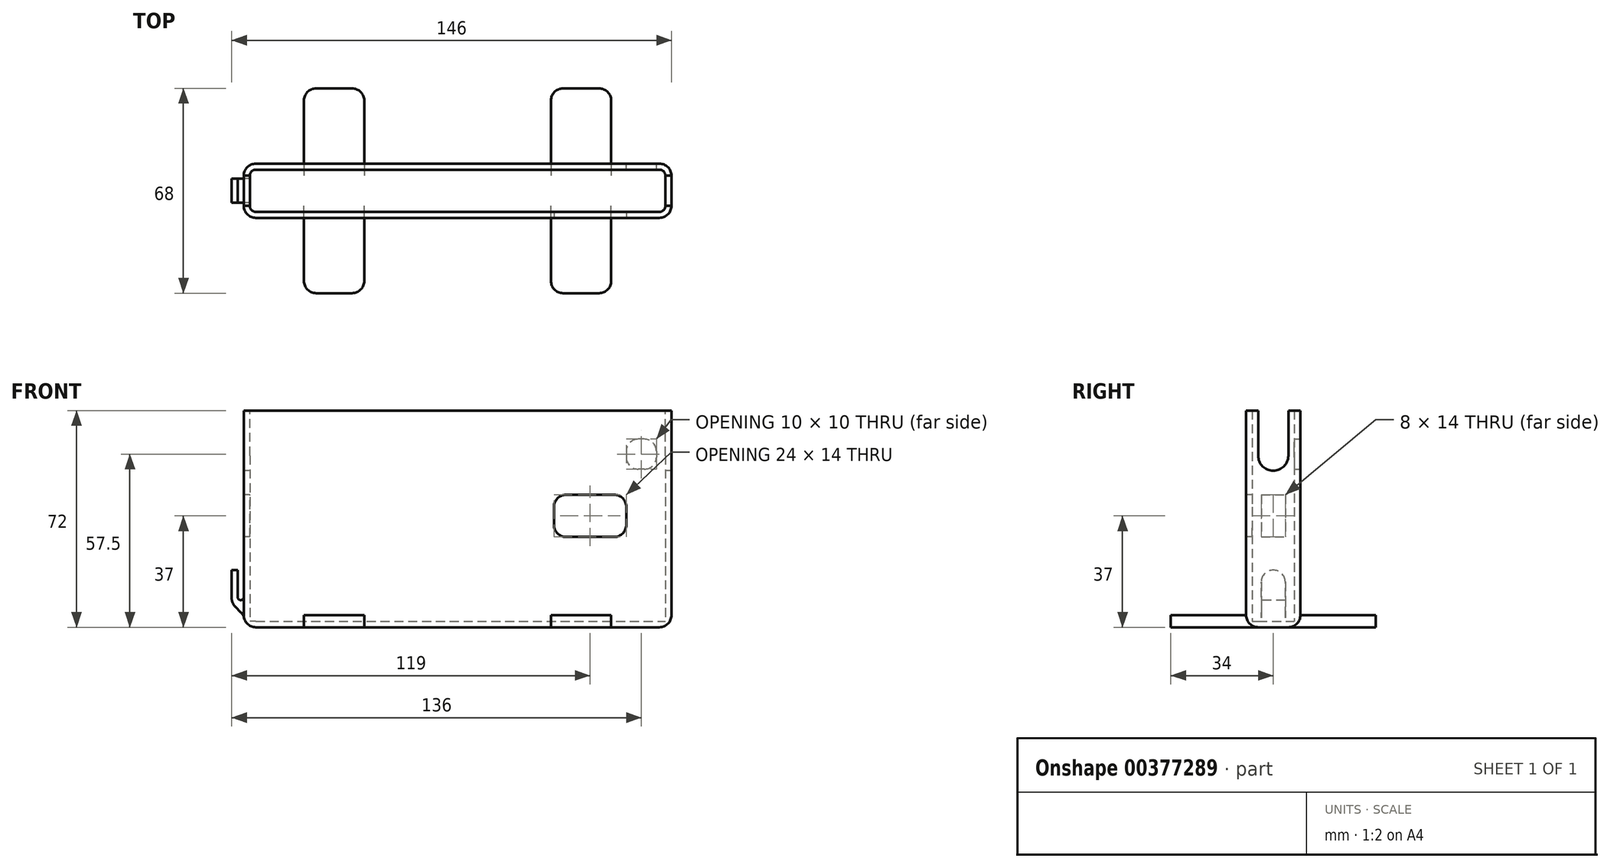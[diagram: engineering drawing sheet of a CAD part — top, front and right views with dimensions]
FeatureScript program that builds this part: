
annotation { "Feature Type Name" : "Feature", "Feature Type Description" : "" }
export const myFeature = defineFeature(function(context is Context, id is Id, definition is map)
    precondition{}
    {
        {
            var Q0;
            Q0=qCreatedBy(makeId("Top.planeOp"),FACE);
            var sketch = newSketch(context, id + "F0", { "sketchPlane" : qUnion([Q0])});
            skLineSegment(sketch, "E0.bottom", {"start": v(0, 0) * mm, "end": v(142, 0) * mm});
            skLineSegment(sketch, "E0.top", {"start": v(0, 18) * mm, "end": v(142, 18) * mm});
            skLineSegment(sketch, "E0.left", {"start": v(0, 0) * mm, "end": v(0, 18) * mm});
            skLineSegment(sketch, "E0.right", {"start": v(142, 0) * mm, "end": v(142, 18) * mm});
            skSolve(sketch);
        }
        {
            var Q0;
            Q0=qSketchRegion(id+"F0",true);
            extrude(context, id + "F1", {"entities" : qUnion([Q0]), "depth" : 2 * mm});
        }
        {
            var Q0;
            Q0=makeQuery(id+"F1.opExtrude","CAP_FACE",FACE,{"disambiguationData":[OSD([sQuery(id+"F0.wireOp",EDGE,"E0.bottom"),sQuery(id+"F0.wireOp",EDGE,"E0.top"),sQuery(id+"F0.wireOp",EDGE,"E0.left"),sQuery(id+"F0.wireOp",EDGE,"E0.right")])],"isStart":false});
            var sketch = newSketch(context, id + "F2", { "sketchPlane" : qUnion([Q0])});
            skLineSegment(sketch, "E1.0", {"start": v(0, 18) * mm, "end": v(142, 18) * mm});
            skLineSegment(sketch, "E1.1", {"start": v(0, 0) * mm, "end": v(0, 18) * mm});
            skLineSegment(sketch, "E1.2", {"start": v(0, 0) * mm, "end": v(142, 0) * mm});
            skLineSegment(sketch, "E1.3", {"start": v(142, 0) * mm, "end": v(142, 18) * mm});
            skLineSegment(sketch, "E2.0", {"start": v(2, 16) * mm, "end": v(140, 16) * mm});
            skLineSegment(sketch, "E2.1", {"start": v(2, 2) * mm, "end": v(2, 16) * mm});
            skLineSegment(sketch, "E2.2", {"start": v(2, 2) * mm, "end": v(140, 2) * mm});
            skLineSegment(sketch, "E2.3", {"start": v(140, 2) * mm, "end": v(140, 16) * mm});
            skSolve(sketch);
        }
        {
            var Q0;
            Q0=qSketchRegion(id+"F2",true);
            extrude(context, id + "F3", {"entities" : qUnion([Q0]), "operationType" : NewBodyOperationType.ADD, "depth" : 70 * mm});
        }
        {
            var Q0;
            Q0=makeQuery(id+"F3.opExtrude","SWEPT_EDGE",EDGE,{"disambiguationData":[OSD([sQuery(id+"F2.wireOp",EDGE,"E2.1"),sQuery(id+"F2.wireOp",EDGE,"E2.2")])]});
            var Q1;
            Q1=makeQuery(id+"F3.opExtrude","SWEPT_EDGE",EDGE,{"disambiguationData":[OSD([sQuery(id+"F2.wireOp",EDGE,"E2.0"),sQuery(id+"F2.wireOp",EDGE,"E2.1")])]});
            var Q2;
            Q2=makeQuery(id+"F3.opExtrude","SWEPT_EDGE",EDGE,{"disambiguationData":[OSD([sQuery(id+"F2.wireOp",EDGE,"E2.0"),sQuery(id+"F2.wireOp",EDGE,"E2.3")])]});
            var Q3;
            Q3=makeQuery(id+"F3.opExtrude","SWEPT_EDGE",EDGE,{"disambiguationData":[OSD([sQuery(id+"F2.wireOp",EDGE,"E2.2"),sQuery(id+"F2.wireOp",EDGE,"E2.3")])]});
            var Q4;
            Q4=makeQuery(id+"F3.opExtrude","CAP_EDGE",EDGE,{"disambiguationData":[OSD([sQuery(id+"F2.wireOp",EDGE,"E2.2")])],"isStart":true});
            var Q5;
            Q5=makeQuery(id+"F3.opExtrude","CAP_EDGE",EDGE,{"disambiguationData":[OSD([sQuery(id+"F2.wireOp",EDGE,"E2.3")])],"isStart":true});
            var Q6;
            Q6=makeQuery(id+"F3.opExtrude","CAP_EDGE",EDGE,{"disambiguationData":[OSD([sQuery(id+"F2.wireOp",EDGE,"E2.0")])],"isStart":true});
            var Q7;
            Q7=makeQuery(id+"F3.opExtrude","CAP_EDGE",EDGE,{"disambiguationData":[OSD([sQuery(id+"F2.wireOp",EDGE,"E2.1")])],"isStart":true});
            fillet(context, id + "F4", {"entities" : qUnion([Q0, Q1, Q2, Q3, Q4, Q5, Q6, Q7]), "radius" : 2 * mm, "tangentPropagation" : true, "allowEdgeOverflow" : false});
        }
        {
            var Q0;
            Q0=makeQuery(id+"F3.boolean.opBoolean","MERGE",EDGE,{"derivedFrom":[makeQuery(id+"F1.opExtrude","SWEPT_EDGE",EDGE,{"disambiguationData":[OSD([sQuery(id+"F0.wireOp",EDGE,"E0.bottom"),sQuery(id+"F0.wireOp",EDGE,"E0.left")])]}),makeQuery(id+"F3.opExtrude","SWEPT_EDGE",EDGE,{"disambiguationData":[OSD([sQuery(id+"F2.wireOp",EDGE,"E1.1"),sQuery(id+"F2.wireOp",EDGE,"E1.2")])]})]});
            var Q1;
            Q1=makeQuery(id+"F3.boolean.opBoolean","MERGE",EDGE,{"derivedFrom":[makeQuery(id+"F1.opExtrude","SWEPT_EDGE",EDGE,{"disambiguationData":[OSD([sQuery(id+"F0.wireOp",EDGE,"E0.top"),sQuery(id+"F0.wireOp",EDGE,"E0.left")])]}),makeQuery(id+"F3.opExtrude","SWEPT_EDGE",EDGE,{"disambiguationData":[OSD([sQuery(id+"F2.wireOp",EDGE,"E1.0"),sQuery(id+"F2.wireOp",EDGE,"E1.1")])]})]});
            var Q2;
            Q2=makeQuery(id+"F3.boolean.opBoolean","MERGE",EDGE,{"derivedFrom":[makeQuery(id+"F1.opExtrude","SWEPT_EDGE",EDGE,{"disambiguationData":[OSD([sQuery(id+"F0.wireOp",EDGE,"E0.top"),sQuery(id+"F0.wireOp",EDGE,"E0.right")])]}),makeQuery(id+"F3.opExtrude","SWEPT_EDGE",EDGE,{"disambiguationData":[OSD([sQuery(id+"F2.wireOp",EDGE,"E1.0"),sQuery(id+"F2.wireOp",EDGE,"E1.3")])]})]});
            var Q3;
            Q3=makeQuery(id+"F3.boolean.opBoolean","MERGE",EDGE,{"derivedFrom":[makeQuery(id+"F1.opExtrude","SWEPT_EDGE",EDGE,{"disambiguationData":[OSD([sQuery(id+"F0.wireOp",EDGE,"E0.bottom"),sQuery(id+"F0.wireOp",EDGE,"E0.right")])]}),makeQuery(id+"F3.opExtrude","SWEPT_EDGE",EDGE,{"disambiguationData":[OSD([sQuery(id+"F2.wireOp",EDGE,"E1.2"),sQuery(id+"F2.wireOp",EDGE,"E1.3")])]})]});
            var Q4;
            Q4=makeQuery(id+"F1.opExtrude","CAP_EDGE",EDGE,{"disambiguationData":[OSD([sQuery(id+"F0.wireOp",EDGE,"E0.bottom")])],"isStart":true});
            var Q5;
            Q5=makeQuery(id+"F1.opExtrude","CAP_EDGE",EDGE,{"disambiguationData":[OSD([sQuery(id+"F0.wireOp",EDGE,"E0.left")])],"isStart":true});
            var Q6;
            Q6=makeQuery(id+"F1.opExtrude","CAP_EDGE",EDGE,{"disambiguationData":[OSD([sQuery(id+"F0.wireOp",EDGE,"E0.top")])],"isStart":true});
            var Q7;
            Q7=makeQuery(id+"F1.opExtrude","CAP_EDGE",EDGE,{"disambiguationData":[OSD([sQuery(id+"F0.wireOp",EDGE,"E0.right")])],"isStart":true});
            fillet(context, id + "F5", {"entities" : qUnion([Q0, Q1, Q2, Q3, Q4, Q5, Q6, Q7]), "radius" : 4 * mm, "tangentPropagation" : true, "allowEdgeOverflow" : false});
        }
        {
            var Q0;
            Q0=makeQuery(id+"F3.boolean.opBoolean","MERGE",FACE,{"derivedFrom":[makeQuery(id+"F1.opExtrude","SWEPT_FACE",FACE,{"disambiguationData":[OSD([sQuery(id+"F0.wireOp",EDGE,"E0.left")])]}),makeQuery(id+"F3.opExtrude","SWEPT_FACE",FACE,{"disambiguationData":[OSD([sQuery(id+"F2.wireOp",EDGE,"E1.1")])]})]});
            var sketch = newSketch(context, id + "F6", { "sketchPlane" : qUnion([Q0])});
            skLineSegment(sketch, "E3", {"start": v(-9, 72) * mm, "end": v(-9, 57) * mm, "construction": true});
            skArc(sketch, "E4.0.startCap", {"start": v(-14, 72) * mm, "mid": v(-9, 77) * mm, "end": v(-4, 72) * mm});
            skArc(sketch, "E4.0.endCap", {"start": v(-4, 57) * mm, "mid": v(-9, 52) * mm, "end": v(-14, 57) * mm});
            skLineSegment(sketch, "E4.0.left", {"start": v(-4, 72) * mm, "end": v(-4, 57) * mm});
            skLineSegment(sketch, "E4.0.right", {"start": v(-14, 72) * mm, "end": v(-14, 57) * mm});
            skSolve(sketch);
        }
        {
            var Q0;
            Q0=qSketchRegion(id+"F6",true);
            extrude(context, id + "F7", {"entities" : qUnion([Q0]), "operationType" : NewBodyOperationType.REMOVE, "endBound" : BoundingType.THROUGH_ALL, "oppositeDirection" : true, "depth" : 25 * mm});
        }
        {
            var Q0;
            Q0=makeQuery(id+"F3.boolean.opBoolean","MERGE",FACE,{"derivedFrom":[makeQuery(id+"F1.opExtrude","SWEPT_FACE",FACE,{"disambiguationData":[OSD([sQuery(id+"F0.wireOp",EDGE,"E0.bottom")])]}),makeQuery(id+"F3.opExtrude","SWEPT_FACE",FACE,{"disambiguationData":[OSD([sQuery(id+"F2.wireOp",EDGE,"E1.2")])]})]});
            var sketch = newSketch(context, id + "F8", { "sketchPlane" : qUnion([Q0])});
            skLineSegment(sketch, "E5.bottom", {"start": v(107, 44) * mm, "end": v(123, 44) * mm});
            skLineSegment(sketch, "E5.top", {"start": v(107, 30) * mm, "end": v(123, 30) * mm});
            skLineSegment(sketch, "E5.left", {"start": v(103, 40) * mm, "end": v(103, 34) * mm});
            skLineSegment(sketch, "E5.right", {"start": v(127, 40) * mm, "end": v(127, 34) * mm});
            skPoint(sketch, "E6", {"position": v(103, 37) * mm});
            skPoint(sketch, "E7.visualSharp", {"position": v(103, 44) * mm});
            skArc(sketch, "E7.filletArc", {"start": v(107, 44) * mm, "mid": v(104.17, 42.83) * mm, "end": v(103, 40) * mm});
            skPoint(sketch, "E8.visualSharp", {"position": v(127, 44) * mm});
            skArc(sketch, "E8.filletArc", {"start": v(127, 40) * mm, "mid": v(125.83, 42.83) * mm, "end": v(123, 44) * mm});
            skPoint(sketch, "E9.visualSharp", {"position": v(127, 30) * mm});
            skArc(sketch, "E9.filletArc", {"start": v(123, 30) * mm, "mid": v(125.83, 31.17) * mm, "end": v(127, 34) * mm});
            skPoint(sketch, "E10.visualSharp", {"position": v(103, 30) * mm});
            skArc(sketch, "E10.filletArc", {"start": v(103, 34) * mm, "mid": v(104.17, 31.17) * mm, "end": v(107, 30) * mm});
            skPoint(sketch, "E11", {"position": v(115, 44) * mm});
            skSolve(sketch);
        }
        {
            var Q0;
            Q0=qSketchRegion(id+"F8",true);
            extrude(context, id + "F9", {"entities" : qUnion([Q0]), "operationType" : NewBodyOperationType.REMOVE, "endBound" : BoundingType.UP_TO_NEXT, "oppositeDirection" : true, "depth" : 25 * mm});
        }
        {
            var Q0;
            Q0=makeQuery(id+"F3.boolean.opBoolean","MERGE",FACE,{"derivedFrom":[makeQuery(id+"F1.opExtrude","SWEPT_FACE",FACE,{"disambiguationData":[OSD([sQuery(id+"F0.wireOp",EDGE,"E0.left")])]}),makeQuery(id+"F3.opExtrude","SWEPT_FACE",FACE,{"disambiguationData":[OSD([sQuery(id+"F2.wireOp",EDGE,"E1.1")])]})]});
            var sketch = newSketch(context, id + "F10", { "sketchPlane" : qUnion([Q0])});
            skLineSegment(sketch, "E12.bottom", {"start": v(-13, 19) * mm, "end": v(-5, 19) * mm});
            skLineSegment(sketch, "E12.top", {"start": v(-13, 4) * mm, "end": v(-5, 4) * mm});
            skLineSegment(sketch, "E12.left", {"start": v(-13, 19) * mm, "end": v(-13, 4) * mm});
            skLineSegment(sketch, "E12.right", {"start": v(-5, 19) * mm, "end": v(-5, 4) * mm});
            skPoint(sketch, "E13", {"position": v(-9, 4) * mm});
            skSolve(sketch);
        }
        {
            var Q0;
            Q0=qSketchRegion(id+"F10",true);
            extrude(context, id + "F11", {"entities" : qUnion([Q0]), "operationType" : NewBodyOperationType.ADD, "depth" : 4 * mm});
        }
        {
            var Q0;
            Q0=makeQuery(id+"F11.opExtrude","CAP_EDGE",EDGE,{"disambiguationData":[OSD([sQuery(id+"F10.wireOp",EDGE,"E12.top")])],"isStart":false});
            chamfer(context, id + "F12", {"entities" : qUnion([Q0]), "width" : 4 * mm, "tangentPropagation" : true});
        }
        {
            var Q0;
            Q0=makeQuery(id+"F11.opExtrude","SWEPT_FACE",FACE,{"disambiguationData":[OSD([sQuery(id+"F10.wireOp",EDGE,"E12.bottom")])]});
            var sketch = newSketch(context, id + "F13", { "sketchPlane" : qUnion([Q0])});
            skLineSegment(sketch, "E14.bottom", {"start": v(-2, 13) * mm, "end": v(0, 13) * mm});
            skLineSegment(sketch, "E14.top", {"start": v(-2, 5) * mm, "end": v(0, 5) * mm});
            skLineSegment(sketch, "E14.left", {"start": v(0, 5) * mm, "end": v(0, 13) * mm});
            skLineSegment(sketch, "E14.right", {"start": v(-2, 5) * mm, "end": v(-2, 13) * mm});
            skSolve(sketch);
        }
        {
            var Q0;
            Q0=qSketchRegion(id+"F13",true);
            extrude(context, id + "F14", {"entities" : qUnion([Q0]), "operationType" : NewBodyOperationType.REMOVE, "oppositeDirection" : true, "depth" : 10 * mm});
        }
        {
            var Q0;
            Q0=makeQuery(id+"F11.opExtrude","SWEPT_EDGE",EDGE,{"disambiguationData":[OSD([sQuery(id+"F10.wireOp",EDGE,"E12.bottom"),sQuery(id+"F10.wireOp",EDGE,"E12.left")])]});
            var Q1;
            Q1=makeQuery(id+"F11.opExtrude","SWEPT_EDGE",EDGE,{"disambiguationData":[OSD([sQuery(id+"F10.wireOp",EDGE,"E12.bottom"),sQuery(id+"F10.wireOp",EDGE,"E12.right")])]});
            var Q2;
            {var subQ0=sQuery(id+"F10.wireOp",EDGE,"E12.top");Q2=makeQuery(id+"F12.opChamfer","BLEND_EDGE",EDGE,{"blendedFrom":[makeQuery(id+"F11.opExtrude","CAP_EDGE",EDGE,{"disambiguationData":[OSD([subQ0])],"isStart":false}),makeQuery(id+"F11.opExtrude","CAP_FACE",FACE,{"disambiguationData":[OSD([sQuery(id+"F10.wireOp",EDGE,"E12.bottom"),subQ0,sQuery(id+"F10.wireOp",EDGE,"E12.left"),sQuery(id+"F10.wireOp",EDGE,"E12.right")])],"isStart":false})],"blendedInto":[makeQuery(id+"F11.opExtrude","CAP_FACE",FACE,{"disambiguationData":[OSD([sQuery(id+"F10.wireOp",EDGE,"E12.bottom"),subQ0,sQuery(id+"F10.wireOp",EDGE,"E12.left"),sQuery(id+"F10.wireOp",EDGE,"E12.right")])],"isStart":false})]});}
            var Q3;
            Q3=makeQuery(id+"F12.opChamfer","BLEND_EDGE",EDGE,{"blendedFrom":[makeQuery(id+"F11.opExtrude","CAP_EDGE",EDGE,{"disambiguationData":[OSD([sQuery(id+"F10.wireOp",EDGE,"E12.top")])],"isStart":false}),makeQuery(id+"F5.opFillet","BLEND_FACE",FACE,{"disambiguationData":[OSD([sQuery(id+"F0.wireOp",EDGE,"E0.right")])]})],"blendedInto":[makeQuery(id+"F5.opFillet","BLEND_FACE",FACE,{"disambiguationData":[OSD([sQuery(id+"F0.wireOp",EDGE,"E0.right")])]})]});
            var Q4;
            Q4=makeQuery(id+"F12.opChamfer","BLEND_EDGE",EDGE,{"blendedFrom":[makeQuery(id+"F11.opExtrude","CAP_EDGE",EDGE,{"disambiguationData":[OSD([sQuery(id+"F10.wireOp",EDGE,"E12.top")])],"isStart":false}),makeQuery(id+"F5.opFillet","BLEND_FACE",FACE,{"disambiguationData":[OSD([sQuery(id+"F0.wireOp",EDGE,"E0.left")])]})],"blendedInto":[makeQuery(id+"F5.opFillet","BLEND_FACE",FACE,{"disambiguationData":[OSD([sQuery(id+"F0.wireOp",EDGE,"E0.left")])]})]});
            fillet(context, id + "F15", {"entities" : qUnion([Q0, Q1, Q2, Q3, Q4]), "radius" : 4 * mm, "tangentPropagation" : true, "allowEdgeOverflow" : false});
        }
        {
            var Q0;
            Q0=makeQuery(id+"F14.boolean.opBoolean","COPY",EDGE,{"derivedFrom":makeQuery(id+"F14.opExtrude","CAP_EDGE",EDGE,{"disambiguationData":[OSD([sQuery(id+"F13.wireOp",EDGE,"E14.right")])],"isStart":false})});
            var Q1;
            Q1=makeQuery(id+"F14.boolean.opBoolean","COPY",EDGE,{"derivedFrom":makeQuery(id+"F14.opExtrude","CAP_EDGE",EDGE,{"disambiguationData":[OSD([sQuery(id+"F13.wireOp",EDGE,"E14.left")])],"isStart":false})});
            fillet(context, id + "F16", {"entities" : qUnion([Q0, Q1]), "radius" : 1 * mm, "tangentPropagation" : true, "allowEdgeOverflow" : false});
        }
        {
            var Q0;
            Q0=makeQuery(id+"F3.boolean.opBoolean","MERGE",FACE,{"derivedFrom":[makeQuery(id+"F1.opExtrude","SWEPT_FACE",FACE,{"disambiguationData":[OSD([sQuery(id+"F0.wireOp",EDGE,"E0.top")])]}),makeQuery(id+"F3.opExtrude","SWEPT_FACE",FACE,{"disambiguationData":[OSD([sQuery(id+"F2.wireOp",EDGE,"E1.0")])]})]});
            var sketch = newSketch(context, id + "F17", { "sketchPlane" : qUnion([Q0])});
            skLineSegment(sketch, "E15.bottom", {"start": v(-133, 62.5) * mm, "end": v(-131, 62.5) * mm});
            skLineSegment(sketch, "E15.top", {"start": v(-133, 52.5) * mm, "end": v(-131, 52.5) * mm});
            skLineSegment(sketch, "E15.left", {"start": v(-137, 58.5) * mm, "end": v(-137, 56.5) * mm});
            skLineSegment(sketch, "E15.right", {"start": v(-127, 58.5) * mm, "end": v(-127, 56.5) * mm});
            skPoint(sketch, "E16.visualSharp", {"position": v(-137, 62.5) * mm});
            skArc(sketch, "E16.filletArc", {"start": v(-133, 62.5) * mm, "mid": v(-135.83, 61.33) * mm, "end": v(-137, 58.5) * mm});
            skPoint(sketch, "E17.visualSharp", {"position": v(-127, 62.5) * mm});
            skArc(sketch, "E17.filletArc", {"start": v(-127, 58.5) * mm, "mid": v(-128.17, 61.33) * mm, "end": v(-131, 62.5) * mm});
            skPoint(sketch, "E18.visualSharp", {"position": v(-127, 52.5) * mm});
            skArc(sketch, "E18.filletArc", {"start": v(-131, 52.5) * mm, "mid": v(-128.17, 53.67) * mm, "end": v(-127, 56.5) * mm});
            skPoint(sketch, "E19.visualSharp", {"position": v(-137, 52.5) * mm});
            skArc(sketch, "E19.filletArc", {"start": v(-137, 56.5) * mm, "mid": v(-135.83, 53.67) * mm, "end": v(-133, 52.5) * mm});
            skPoint(sketch, "E20", {"position": v(-132, 62.5) * mm});
            skPoint(sketch, "E21", {"position": v(-127, 57.5) * mm});
            skSolve(sketch);
        }
        {
            var Q0;
            Q0=qSketchRegion(id+"F17",true);
            extrude(context, id + "F18", {"entities" : qUnion([Q0]), "operationType" : NewBodyOperationType.REMOVE, "endBound" : BoundingType.UP_TO_NEXT, "oppositeDirection" : true, "depth" : 25 * mm});
        }
        {
            var Q0;
            Q0=makeQuery(id+"F3.boolean.opBoolean","MERGE",FACE,{"derivedFrom":[makeQuery(id+"F1.opExtrude","SWEPT_FACE",FACE,{"disambiguationData":[OSD([sQuery(id+"F0.wireOp",EDGE,"E0.left")])]}),makeQuery(id+"F3.opExtrude","SWEPT_FACE",FACE,{"disambiguationData":[OSD([sQuery(id+"F2.wireOp",EDGE,"E1.1")])]})]});
            var sketch = newSketch(context, id + "F19", { "sketchPlane" : qUnion([Q0])});
            skLineSegment(sketch, "E22.bottom", {"start": v(-5, 44) * mm, "end": v(-13, 44) * mm});
            skLineSegment(sketch, "E22.top", {"start": v(-5, 30) * mm, "end": v(-13, 30) * mm});
            skLineSegment(sketch, "E22.left", {"start": v(-5, 44) * mm, "end": v(-5, 30) * mm});
            skLineSegment(sketch, "E22.right", {"start": v(-13, 44) * mm, "end": v(-13, 30) * mm});
            skPoint(sketch, "E22.middle", {"position": v(-9, 37) * mm});
            skLineSegment(sketch, "E23", {"start": v(-14, 30.5) * mm, "end": v(-4, 30.5) * mm, "construction": true});
            skPoint(sketch, "E24", {"position": v(-9, 30.5) * mm});
            skSolve(sketch);
        }
        {
            var Q0;
            Q0=qSketchRegion(id+"F19",true);
            extrude(context, id + "F20", {"entities" : qUnion([Q0]), "operationType" : NewBodyOperationType.REMOVE, "endBound" : BoundingType.UP_TO_NEXT, "oppositeDirection" : true, "depth" : 25 * mm});
        }
        {
            var Q0;
            Q0=makeQuery(id+"F3.boolean.opBoolean","MERGE",FACE,{"derivedFrom":[makeQuery(id+"F1.opExtrude","SWEPT_FACE",FACE,{"disambiguationData":[OSD([sQuery(id+"F0.wireOp",EDGE,"E0.top")])]}),makeQuery(id+"F3.opExtrude","SWEPT_FACE",FACE,{"disambiguationData":[OSD([sQuery(id+"F2.wireOp",EDGE,"E1.0")])]})]});
            var sketch = newSketch(context, id + "F21", { "sketchPlane" : qUnion([Q0])});
            skLineSegment(sketch, "E25.bottom", {"start": v(-122, 4) * mm, "end": v(-102, 4) * mm});
            skLineSegment(sketch, "E25.top", {"start": v(-122, 0) * mm, "end": v(-102, 0) * mm});
            skLineSegment(sketch, "E25.left", {"start": v(-122, 4) * mm, "end": v(-122, 0) * mm});
            skLineSegment(sketch, "E25.right", {"start": v(-102, 4) * mm, "end": v(-102, 0) * mm});
            skLineSegment(sketch, "E26.bottom", {"start": v(-40, 4) * mm, "end": v(-20, 4) * mm});
            skLineSegment(sketch, "E26.top", {"start": v(-40, 0) * mm, "end": v(-20, 0) * mm});
            skLineSegment(sketch, "E26.left", {"start": v(-40, 4) * mm, "end": v(-40, 0) * mm});
            skLineSegment(sketch, "E26.right", {"start": v(-20, 4) * mm, "end": v(-20, 0) * mm});
            skSolve(sketch);
        }
        {
            var Q0;
            Q0 = qSketchRegion(id + "F21", true);
            var Q1;
            Q1=makeQuery(id+"F1.opExtrude","SWEPT_BODY",BODY,{"disambiguationData":[OSD([sQuery(id+"F0.wireOp",EDGE,"E0.bottom"),sQuery(id+"F0.wireOp",EDGE,"E0.top"),sQuery(id+"F0.wireOp",EDGE,"E0.left"),sQuery(id+"F0.wireOp",EDGE,"E0.right")])]});
            extrude(context, id + "F22", {"entities" : qUnion([Q0]), "operationType" : NewBodyOperationType.ADD, "depth" : 25 * mm, "hasSecondDirection" : true, "secondDirectionBound" : SecondDirectionBoundingType.UP_TO_BODY, "secondDirectionOppositeDirection" : true, "secondDirectionBoundEntityBody" : qUnion([Q1]), "secondDirectionDepth" : 25 * mm});
        }
        {
            var Q0;
            Q0=makeQuery(id+"F3.boolean.opBoolean","MERGE",FACE,{"derivedFrom":[makeQuery(id+"F1.opExtrude","SWEPT_FACE",FACE,{"disambiguationData":[OSD([sQuery(id+"F0.wireOp",EDGE,"E0.bottom")])]}),makeQuery(id+"F3.opExtrude","SWEPT_FACE",FACE,{"disambiguationData":[OSD([sQuery(id+"F2.wireOp",EDGE,"E1.2")])]})]});
            var sketch = newSketch(context, id + "F23", { "sketchPlane" : qUnion([Q0])});
            skLineSegment(sketch, "E27.bottom", {"start": v(20, 4) * mm, "end": v(40, 4) * mm});
            skLineSegment(sketch, "E27.top", {"start": v(20, 0) * mm, "end": v(40, 0) * mm});
            skLineSegment(sketch, "E27.left", {"start": v(20, 4) * mm, "end": v(20, 0) * mm});
            skLineSegment(sketch, "E27.right", {"start": v(40, 4) * mm, "end": v(40, 0) * mm});
            skLineSegment(sketch, "E28.bottom", {"start": v(102, 4) * mm, "end": v(122, 4) * mm});
            skLineSegment(sketch, "E28.top", {"start": v(102, 0) * mm, "end": v(122, 0) * mm});
            skLineSegment(sketch, "E28.left", {"start": v(102, 4) * mm, "end": v(102, 0) * mm});
            skLineSegment(sketch, "E28.right", {"start": v(122, 4) * mm, "end": v(122, 0) * mm});
            skSolve(sketch);
        }
        {
            var Q0;
            Q0 = qSketchRegion(id + "F23", true);
            var Q1;
            Q1=makeQuery(id+"F1.opExtrude","SWEPT_BODY",BODY,{"disambiguationData":[OSD([sQuery(id+"F0.wireOp",EDGE,"E0.bottom"),sQuery(id+"F0.wireOp",EDGE,"E0.top"),sQuery(id+"F0.wireOp",EDGE,"E0.left"),sQuery(id+"F0.wireOp",EDGE,"E0.right")])]});
            extrude(context, id + "F24", {"entities" : qUnion([Q0]), "operationType" : NewBodyOperationType.ADD, "depth" : 25 * mm, "hasSecondDirection" : true, "secondDirectionBound" : SecondDirectionBoundingType.UP_TO_BODY, "secondDirectionOppositeDirection" : true, "secondDirectionBoundEntityBody" : qUnion([Q1]), "secondDirectionDepth" : 25 * mm});
        }
        {
            var Q0;
            {var subQ0=sQuery(id+"F23.wireOp",EDGE,"E27.left");Q0=makeQuery(id+"F24.opExtrude","CAP_EDGE",EDGE,{"disambiguationData":[OSD([subQ0]),topologyDisambiguationEdgeConnected([makeQuery(id+"F23.imprint","IMPRINT",EDGE,{"derivedFrom":sQuery(id+"F23.wireOp",EDGE,"E27.bottom")})])],"isStart":false});}
            var Q1;
            {var subQ0=sQuery(id+"F23.wireOp",EDGE,"E27.right");Q1=makeQuery(id+"F24.opExtrude","CAP_EDGE",EDGE,{"disambiguationData":[OSD([subQ0]),topologyDisambiguationEdgeConnected([makeQuery(id+"F23.imprint","IMPRINT",EDGE,{"derivedFrom":sQuery(id+"F23.wireOp",EDGE,"E27.bottom")})])],"isStart":false});}
            var Q2;
            {var subQ0=sQuery(id+"F23.wireOp",EDGE,"E28.left");Q2=makeQuery(id+"F24.opExtrude","CAP_EDGE",EDGE,{"disambiguationData":[OSD([subQ0]),topologyDisambiguationEdgeConnected([makeQuery(id+"F23.imprint","IMPRINT",EDGE,{"derivedFrom":sQuery(id+"F23.wireOp",EDGE,"E28.bottom")})])],"isStart":false});}
            var Q3;
            {var subQ0=sQuery(id+"F23.wireOp",EDGE,"E28.right");Q3=makeQuery(id+"F24.opExtrude","CAP_EDGE",EDGE,{"disambiguationData":[OSD([subQ0]),topologyDisambiguationEdgeConnected([makeQuery(id+"F23.imprint","IMPRINT",EDGE,{"derivedFrom":sQuery(id+"F23.wireOp",EDGE,"E28.bottom")})])],"isStart":false});}
            var Q4;
            {var subQ0=sQuery(id+"F21.wireOp",EDGE,"E26.right");Q4=makeQuery(id+"F22.opExtrude","CAP_EDGE",EDGE,{"disambiguationData":[OSD([subQ0]),topologyDisambiguationEdgeConnected([makeQuery(id+"F21.imprint","IMPRINT",EDGE,{"derivedFrom":sQuery(id+"F21.wireOp",EDGE,"E26.bottom")})])],"isStart":false});}
            var Q5;
            {var subQ0=sQuery(id+"F21.wireOp",EDGE,"E26.left");Q5=makeQuery(id+"F22.opExtrude","CAP_EDGE",EDGE,{"disambiguationData":[OSD([subQ0]),topologyDisambiguationEdgeConnected([makeQuery(id+"F21.imprint","IMPRINT",EDGE,{"derivedFrom":sQuery(id+"F21.wireOp",EDGE,"E26.bottom")})])],"isStart":false});}
            var Q6;
            {var subQ0=sQuery(id+"F21.wireOp",EDGE,"E25.right");Q6=makeQuery(id+"F22.opExtrude","CAP_EDGE",EDGE,{"disambiguationData":[OSD([subQ0]),topologyDisambiguationEdgeConnected([makeQuery(id+"F21.imprint","IMPRINT",EDGE,{"derivedFrom":sQuery(id+"F21.wireOp",EDGE,"E25.bottom")})])],"isStart":false});}
            var Q7;
            {var subQ0=sQuery(id+"F21.wireOp",EDGE,"E25.left");Q7=makeQuery(id+"F22.opExtrude","CAP_EDGE",EDGE,{"disambiguationData":[OSD([subQ0]),topologyDisambiguationEdgeConnected([makeQuery(id+"F21.imprint","IMPRINT",EDGE,{"derivedFrom":sQuery(id+"F21.wireOp",EDGE,"E25.bottom")})])],"isStart":false});}
            fillet(context, id + "F25", {"entities" : qUnion([Q0, Q1, Q2, Q3, Q4, Q5, Q6, Q7]), "radius" : 4 * mm, "tangentPropagation" : true, "allowEdgeOverflow" : false});
        }
    });
